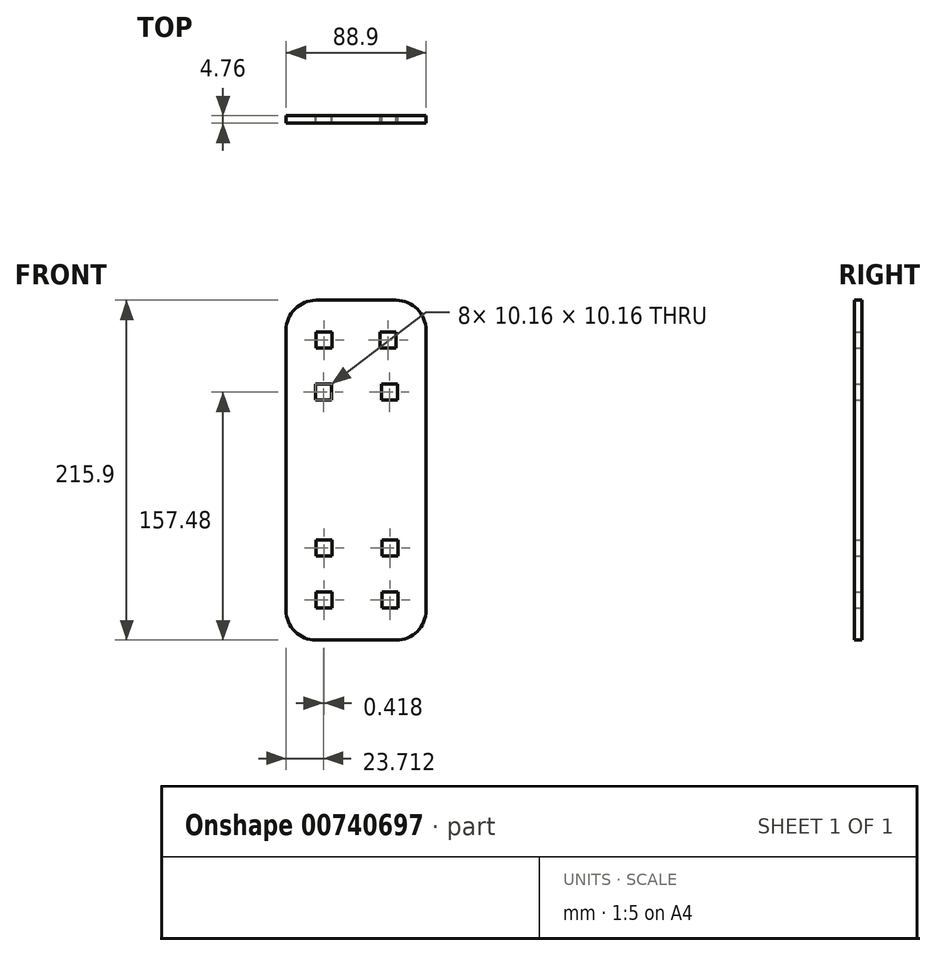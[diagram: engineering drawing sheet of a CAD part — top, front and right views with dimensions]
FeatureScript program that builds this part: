
annotation { "Feature Type Name" : "Feature", "Feature Type Description" : "" }
export const myFeature = defineFeature(function(context is Context, id is Id, definition is map)
    precondition{}
    {
        {
            var Q0;
            Q0=qCreatedBy(makeId("Front.planeOp"),FACE);
            var sketch = newSketch(context, id + "F0", { "sketchPlane" : qUnion([Q0])});
            skLineSegment(sketch, "E0.bottom", {"start": v(-25.4, 107.95) * mm, "end": v(25.4, 107.95) * mm});
            skLineSegment(sketch, "E0.top", {"start": v(-25.4, -107.95) * mm, "end": v(25.4, -107.95) * mm});
            skLineSegment(sketch, "E0.left", {"start": v(-44.45, 88.9) * mm, "end": v(-44.45, -88.9) * mm});
            skLineSegment(sketch, "E0.right", {"start": v(44.45, 88.9) * mm, "end": v(44.45, -88.9) * mm});
            skPoint(sketch, "E1.visualSharp", {"position": v(-44.45, 107.95) * mm});
            skArc(sketch, "E1.filletArc", {"start": v(-25.4, 107.95) * mm, "mid": v(-38.87, 102.37) * mm, "end": v(-44.45, 88.9) * mm});
            skPoint(sketch, "E2.visualSharp", {"position": v(44.45, 107.95) * mm});
            skArc(sketch, "E2.filletArc", {"start": v(44.45, 88.9) * mm, "mid": v(38.87, 102.37) * mm, "end": v(25.4, 107.95) * mm});
            skPoint(sketch, "E3.visualSharp", {"position": v(44.45, -107.95) * mm});
            skArc(sketch, "E3.filletArc", {"start": v(25.4, -107.95) * mm, "mid": v(38.87, -102.37) * mm, "end": v(44.45, -88.9) * mm});
            skPoint(sketch, "E4.visualSharp", {"position": v(-44.45, -107.95) * mm});
            skArc(sketch, "E4.filletArc", {"start": v(-44.45, -88.9) * mm, "mid": v(-38.87, -102.37) * mm, "end": v(-25.4, -107.95) * mm});
            skLineSegment(sketch, "E5.bottom", {"start": v(-25.4, 87.63) * mm, "end": v(-15.24, 87.63) * mm});
            skLineSegment(sketch, "E5.top", {"start": v(-25.4, 77.47) * mm, "end": v(-15.24, 77.47) * mm});
            skLineSegment(sketch, "E5.left", {"start": v(-25.4, 87.63) * mm, "end": v(-25.4, 77.47) * mm});
            skLineSegment(sketch, "E5.right", {"start": v(-15.24, 87.63) * mm, "end": v(-15.24, 77.47) * mm});
            skLineSegment(sketch, "E6.bottom", {"start": v(15.24, 87.63) * mm, "end": v(25.4, 87.63) * mm});
            skLineSegment(sketch, "E6.top", {"start": v(15.24, 77.47) * mm, "end": v(25.4, 77.47) * mm});
            skLineSegment(sketch, "E6.left", {"start": v(15.24, 87.63) * mm, "end": v(15.24, 77.47) * mm});
            skLineSegment(sketch, "E6.right", {"start": v(25.4, 87.63) * mm, "end": v(25.4, 77.47) * mm});
            skLineSegment(sketch, "E7.bottom", {"start": v(-25.82, 54.6) * mm, "end": v(-15.66, 54.6) * mm});
            skLineSegment(sketch, "E7.top", {"start": v(-25.82, 44.45) * mm, "end": v(-15.66, 44.45) * mm});
            skLineSegment(sketch, "E7.left", {"start": v(-25.82, 54.6) * mm, "end": v(-25.82, 44.45) * mm});
            skLineSegment(sketch, "E7.right", {"start": v(-15.66, 54.6) * mm, "end": v(-15.66, 44.45) * mm});
            skLineSegment(sketch, "E8.bottom", {"start": v(16.1, 54.61) * mm, "end": v(26.25, 54.61) * mm});
            skLineSegment(sketch, "E8.top", {"start": v(16.1, 44.45) * mm, "end": v(26.25, 44.45) * mm});
            skLineSegment(sketch, "E8.left", {"start": v(16.1, 54.61) * mm, "end": v(16.1, 44.45) * mm});
            skLineSegment(sketch, "E8.right", {"start": v(26.25, 54.61) * mm, "end": v(26.25, 44.45) * mm});
            skLineSegment(sketch, "E9.bottom", {"start": v(-25.4, -77.47) * mm, "end": v(-15.24, -77.47) * mm});
            skLineSegment(sketch, "E9.top", {"start": v(-25.4, -87.63) * mm, "end": v(-15.24, -87.63) * mm});
            skLineSegment(sketch, "E9.left", {"start": v(-25.4, -77.47) * mm, "end": v(-25.4, -87.63) * mm});
            skLineSegment(sketch, "E9.right", {"start": v(-15.24, -77.47) * mm, "end": v(-15.24, -87.63) * mm});
            skLineSegment(sketch, "E10.bottom", {"start": v(16.51, -77.47) * mm, "end": v(26.67, -77.47) * mm});
            skLineSegment(sketch, "E10.top", {"start": v(16.51, -87.63) * mm, "end": v(26.67, -87.63) * mm});
            skLineSegment(sketch, "E10.left", {"start": v(16.51, -77.47) * mm, "end": v(16.51, -87.63) * mm});
            skLineSegment(sketch, "E10.right", {"start": v(26.67, -77.47) * mm, "end": v(26.67, -87.63) * mm});
            skLineSegment(sketch, "E11.bottom", {"start": v(-25.4, -44.45) * mm, "end": v(-15.24, -44.45) * mm});
            skLineSegment(sketch, "E11.top", {"start": v(-25.4, -54.6) * mm, "end": v(-15.24, -54.6) * mm});
            skLineSegment(sketch, "E11.left", {"start": v(-25.4, -44.45) * mm, "end": v(-25.4, -54.6) * mm});
            skLineSegment(sketch, "E11.right", {"start": v(-15.24, -44.45) * mm, "end": v(-15.24, -54.6) * mm});
            skLineSegment(sketch, "E12.bottom", {"start": v(16.51, -44.45) * mm, "end": v(26.67, -44.45) * mm});
            skLineSegment(sketch, "E12.top", {"start": v(16.51, -54.6) * mm, "end": v(26.67, -54.6) * mm});
            skLineSegment(sketch, "E12.left", {"start": v(16.51, -44.45) * mm, "end": v(16.51, -54.6) * mm});
            skLineSegment(sketch, "E12.right", {"start": v(26.67, -44.45) * mm, "end": v(26.67, -54.6) * mm});
            skLineSegment(sketch, "E13", {"start": v(0, 83.02) * mm, "end": v(0, -116.43) * mm, "construction": true});
            skSolve(sketch);
        }
        {
            var Q0;
            Q0=makeQuery(id+"F0.imprint","IMPRINT",FACE,{"disambiguationData":[TD([[makeQuery(id+"F0.imprint","IMPRINT",EDGE,{"derivedFrom":sQuery(id+"F0.wireOp",EDGE,"E0.bottom")}),-1.0]])]});
            extrude(context, id + "F1", {"entities" : qUnion([Q0]), "depth" : 4.76 * mm, "offsetDistance" : 25.4 * mm});
        }
    });
